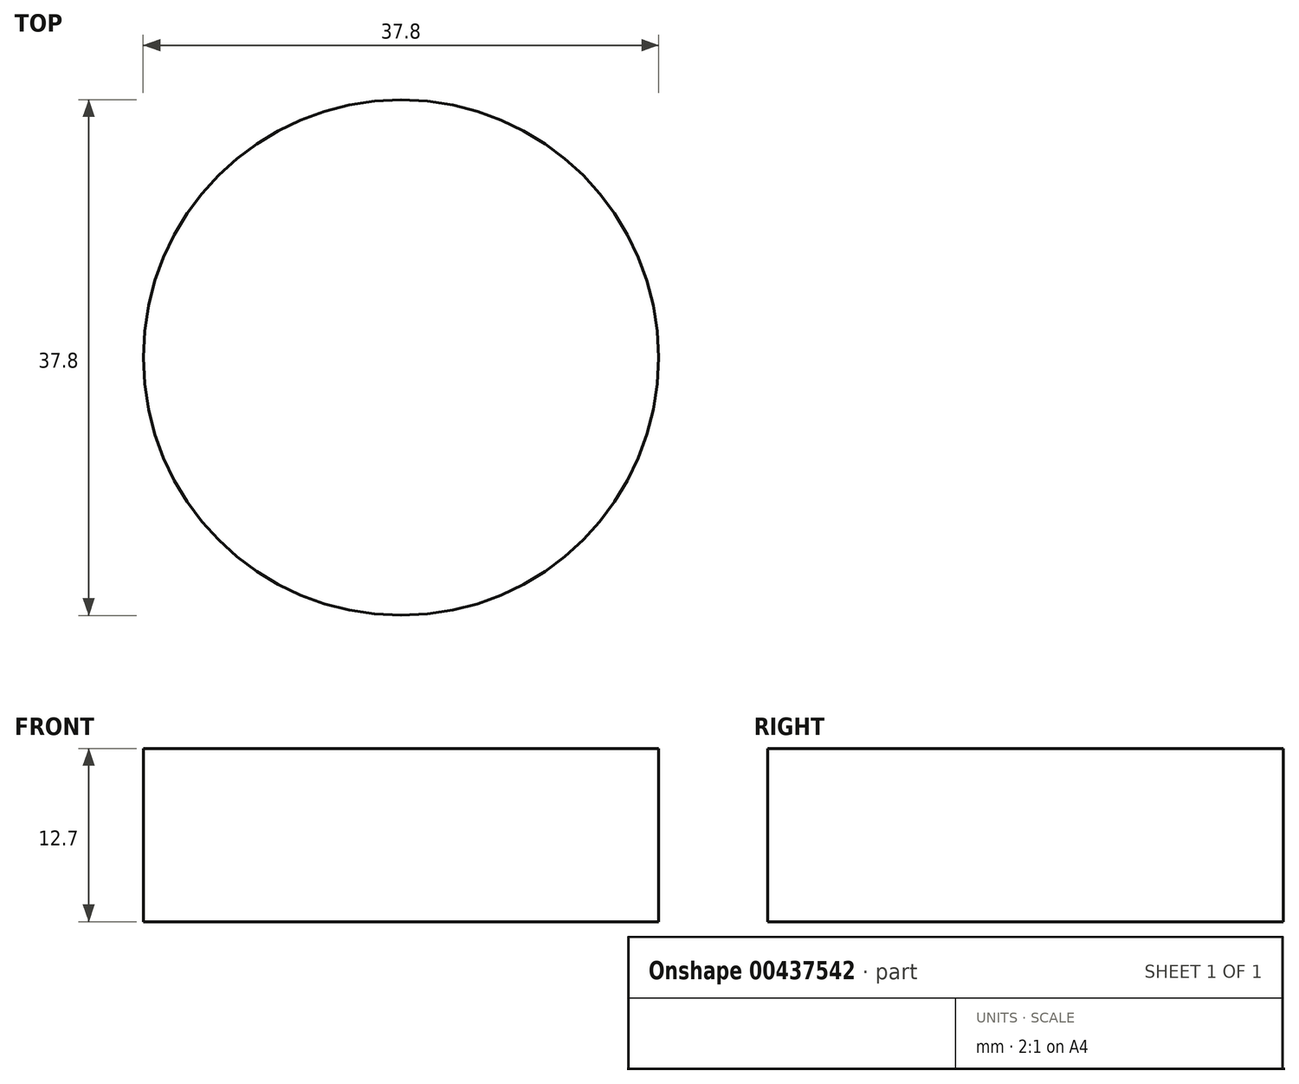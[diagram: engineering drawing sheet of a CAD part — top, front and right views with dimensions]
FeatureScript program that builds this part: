
annotation { "Feature Type Name" : "Feature", "Feature Type Description" : "" }
export const myFeature = defineFeature(function(context is Context, id is Id, definition is map)
    precondition{}
    {
        {
            var Q0;
            Q0=qCreatedBy(makeId("Top.planeOp"),FACE);
            var sketch = newSketch(context, id + "F0", { "sketchPlane" : qUnion([Q0])});
            skCircle(sketch, "E0", {"center": v(0, 0) * mm, "radius": 18.9 * mm});
            skSolve(sketch);
        }
        {
            var Q0;
            Q0=sQuery(id+"F0.wireOp",EDGE,"E0");
            extrude(context, id + "F1", {"bodyType" : ToolBodyType.SURFACE, "surfaceEntities" : qUnion([Q0]), "depth" : 12.7 * mm});
        }
    });
